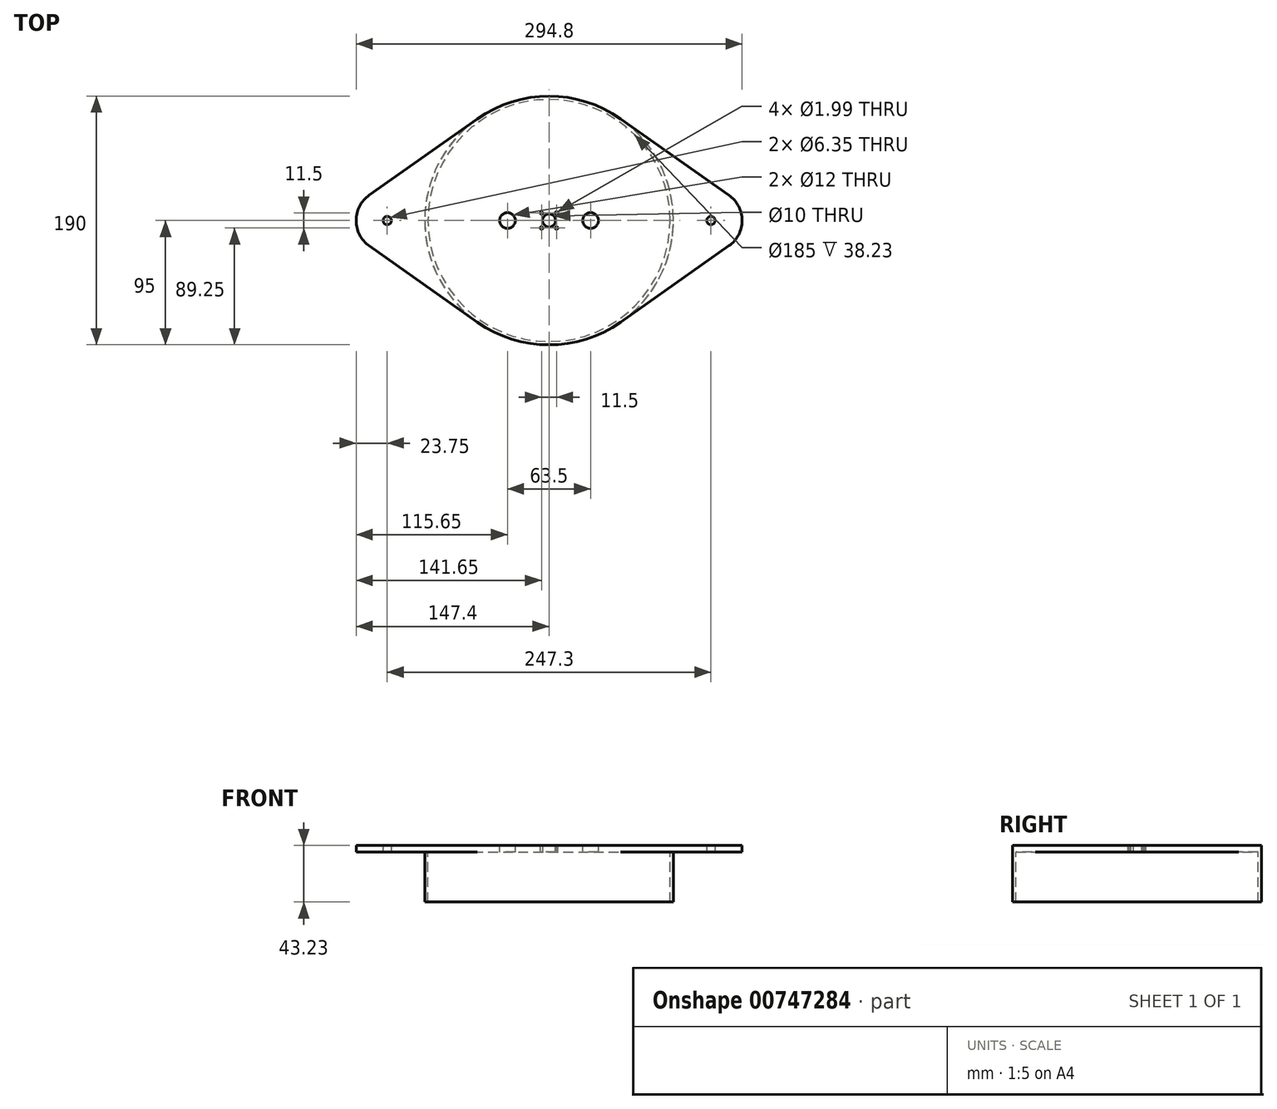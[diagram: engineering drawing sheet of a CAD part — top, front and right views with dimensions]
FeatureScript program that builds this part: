
annotation { "Feature Type Name" : "Feature", "Feature Type Description" : "" }
export const myFeature = defineFeature(function(context is Context, id is Id, definition is map)
    precondition{}
    {
        {
            var Q0;
            Q0=qCreatedBy(makeId("Top.planeOp"),FACE);
            var sketch = newSketch(context, id + "F0", { "sketchPlane" : qUnion([Q0])});
            skCircle(sketch, "E0", {"center": v(0, 0) * mm, "radius": 95 * mm});
            skLineSegment(sketch, "E1", {"start": v(-123.65, 0) * mm, "end": v(123.65, 0) * mm, "construction": true});
            skCircle(sketch, "E2", {"center": v(-123.65, 0) * mm, "radius": 23.75 * mm});
            skCircle(sketch, "E3", {"center": v(123.65, 0) * mm, "radius": 23.75 * mm});
            skCircle(sketch, "E4", {"center": v(0, 0) * mm, "radius": 5 * mm});
            skLineSegment(sketch, "E5", {"start": v(-137.34, 19.41) * mm, "end": v(-54.74, 77.64) * mm});
            skLineSegment(sketch, "E6", {"start": v(137.34, 19.41) * mm, "end": v(54.74, 77.64) * mm});
            skLineSegment(sketch, "E7", {"start": v(-137.34, -19.41) * mm, "end": v(-54.74, -77.64) * mm});
            skLineSegment(sketch, "E8", {"start": v(137.34, -19.41) * mm, "end": v(54.74, -77.64) * mm});
            skCircle(sketch, "E9", {"center": v(-123.65, 0) * mm, "radius": 3.18 * mm});
            skCircle(sketch, "E10", {"center": v(123.65, 0) * mm, "radius": 3.18 * mm});
            skSolve(sketch);
        }
        {
            var Q0;
            Q0=qSketchRegion(id+"F0",true);
            extrude(context, id + "F1", {"entities" : qUnion([Q0]), "depth" : 5 * mm, "offsetDistance" : 25 * mm});
        }
        {
            var Q0;
            Q0=makeQuery(id+"F1.opExtrude","CAP_FACE",FACE,{"disambiguationData":[OSD([sQuery(id+"F0.wireOp",EDGE,"E0"),sQuery(id+"F0.wireOp",EDGE,"E2"),sQuery(id+"F0.wireOp",EDGE,"E3"),sQuery(id+"F0.wireOp",EDGE,"E4"),sQuery(id+"F0.wireOp",EDGE,"E5"),sQuery(id+"F0.wireOp",EDGE,"E6"),sQuery(id+"F0.wireOp",EDGE,"E7"),sQuery(id+"F0.wireOp",EDGE,"E8")])],"isStart":true});
            var sketch = newSketch(context, id + "F2", { "sketchPlane" : qUnion([Q0])});
            skCircle(sketch, "E11", {"center": v(0, 0) * mm, "radius": 95 * mm});
            skCircle(sketch, "E12", {"center": v(0, 0) * mm, "radius": 92.5 * mm});
            skSolve(sketch);
        }
        {
            var Q0;
            Q0=qSketchRegion(id+"F2",true);
            extrude(context, id + "F3", {"entities" : qUnion([Q0]), "operationType" : NewBodyOperationType.ADD, "depth" : 38.23 * mm, "offsetDistance" : 25 * mm});
        }
        {
            var Q0;
            Q0=makeQuery(id+"F1.opExtrude","CAP_FACE",FACE,{"disambiguationData":[OSD([sQuery(id+"F0.wireOp",EDGE,"E0"),sQuery(id+"F0.wireOp",EDGE,"E2"),sQuery(id+"F0.wireOp",EDGE,"E3"),sQuery(id+"F0.wireOp",EDGE,"E4"),sQuery(id+"F0.wireOp",EDGE,"E5"),sQuery(id+"F0.wireOp",EDGE,"E6"),sQuery(id+"F0.wireOp",EDGE,"E7"),sQuery(id+"F0.wireOp",EDGE,"E8")])],"isStart":false});
            var sketch = newSketch(context, id + "F4", { "sketchPlane" : qUnion([Q0])});
            skLineSegment(sketch, "E13.bottom", {"start": v(5.75, 5.75) * mm, "end": v(-5.75, 5.75) * mm, "construction": true});
            skLineSegment(sketch, "E13.top", {"start": v(5.75, -5.75) * mm, "end": v(-5.75, -5.75) * mm, "construction": true});
            skLineSegment(sketch, "E13.left", {"start": v(5.75, 5.75) * mm, "end": v(5.75, -5.75) * mm, "construction": true});
            skLineSegment(sketch, "E13.right", {"start": v(-5.75, 5.75) * mm, "end": v(-5.75, -5.75) * mm, "construction": true});
            skPoint(sketch, "E13.middle", {"position": v(0, 0) * mm});
            skSolve(sketch);
        }
        {
            var Q0;
            Q0=makeQuery(id+"F4.imprint","IMPRINT",FACE,{"disambiguationData":[TD([[makeQuery(id+"F4.imprint","IMPRINT",EDGE,{"derivedFrom":makeQuery(id+"F1.opExtrude","CAP_EDGE",EDGE,{"disambiguationData":[OSD([sQuery(id+"F0.wireOp",EDGE,"E2")])],"isStart":false})}),1.0]])]});
            var sketch = newSketch(context, id + "F5", { "sketchPlane" : qUnion([Q0])});
            skLineSegment(sketch, "E14", {"start": v(-31.75, 0) * mm, "end": v(31.75, 0) * mm, "construction": true});
            skSolve(sketch);
        }
        {
            var Q0;
            Q0=sQuery(id+"F4.wireOp",VERTEX,"E13.right.start");
            var Q1;
            Q1=sQuery(id+"F4.wireOp",VERTEX,"E13.left.start");
            var Q2;
            Q2=sQuery(id+"F4.wireOp",VERTEX,"E13.top.start");
            var Q3;
            Q3=sQuery(id+"F4.wireOp",VERTEX,"E13.top.end");
            var Q4;
            Q4=makeQuery(id+"F1.opExtrude","SWEPT_BODY",BODY,{"disambiguationData":[OSD([sQuery(id+"F0.wireOp",EDGE,"E0"),sQuery(id+"F0.wireOp",EDGE,"E2"),sQuery(id+"F0.wireOp",EDGE,"E3"),sQuery(id+"F0.wireOp",EDGE,"E4"),sQuery(id+"F0.wireOp",EDGE,"E5"),sQuery(id+"F0.wireOp",EDGE,"E6"),sQuery(id+"F0.wireOp",EDGE,"E7"),sQuery(id+"F0.wireOp",EDGE,"E8")])]});
            hole(context, id + "F6", {"style" : HoleStyle.SIMPLE, "endStyle" : HoleEndStyle.BLIND, "standardTappedOrClearance" : lookupTablePath({ "standard" : "ANSI", "engagement" : "75%", "pitch" : "48 tpi", "size" : "#3", "type" : "Tapped" }), "standardBlindInLast" : lookupTablePath({ "standard" : "ANSI", "engagement" : "75%", "pitch" : "48 tpi", "size" : "#3", "type" : "Tapped" }), "holeDiameter" : 2 * mm, "majorDiameter" : 2.5 * mm, "showTappedDepth" : true, "holeDepth" : 13.6 * mm, "isTappedThrough" : true, "tappedDepth" : 12 * mm, "tapClearance" : 3, "locations" : qUnion([Q0, Q1, Q2, Q3]), "scope" : qUnion([Q4])});
        }
        {
            var Q0;
            Q0=sQuery(id+"F5.wireOp",VERTEX,"E14.start");
            var Q1;
            Q1=sQuery(id+"F5.wireOp",VERTEX,"E14.end");
            var Q2;
            Q2=makeQuery(id+"F1.opExtrude","SWEPT_BODY",BODY,{"disambiguationData":[OSD([sQuery(id+"F0.wireOp",EDGE,"E0"),sQuery(id+"F0.wireOp",EDGE,"E2"),sQuery(id+"F0.wireOp",EDGE,"E3"),sQuery(id+"F0.wireOp",EDGE,"E4"),sQuery(id+"F0.wireOp",EDGE,"E5"),sQuery(id+"F0.wireOp",EDGE,"E6"),sQuery(id+"F0.wireOp",EDGE,"E7"),sQuery(id+"F0.wireOp",EDGE,"E8")])]});
            hole(context, id + "F7", {"style" : HoleStyle.SIMPLE, "endStyle" : HoleEndStyle.BLIND, "holeDiameter" : 12 * mm, "majorDiameter" : 2.5 * mm, "holeDepth" : 13.6 * mm, "isTappedThrough" : true, "tappedDepth" : 12 * mm, "tapClearance" : 3, "locations" : qUnion([Q0, Q1]), "scope" : qUnion([Q2])});
        }
    });
